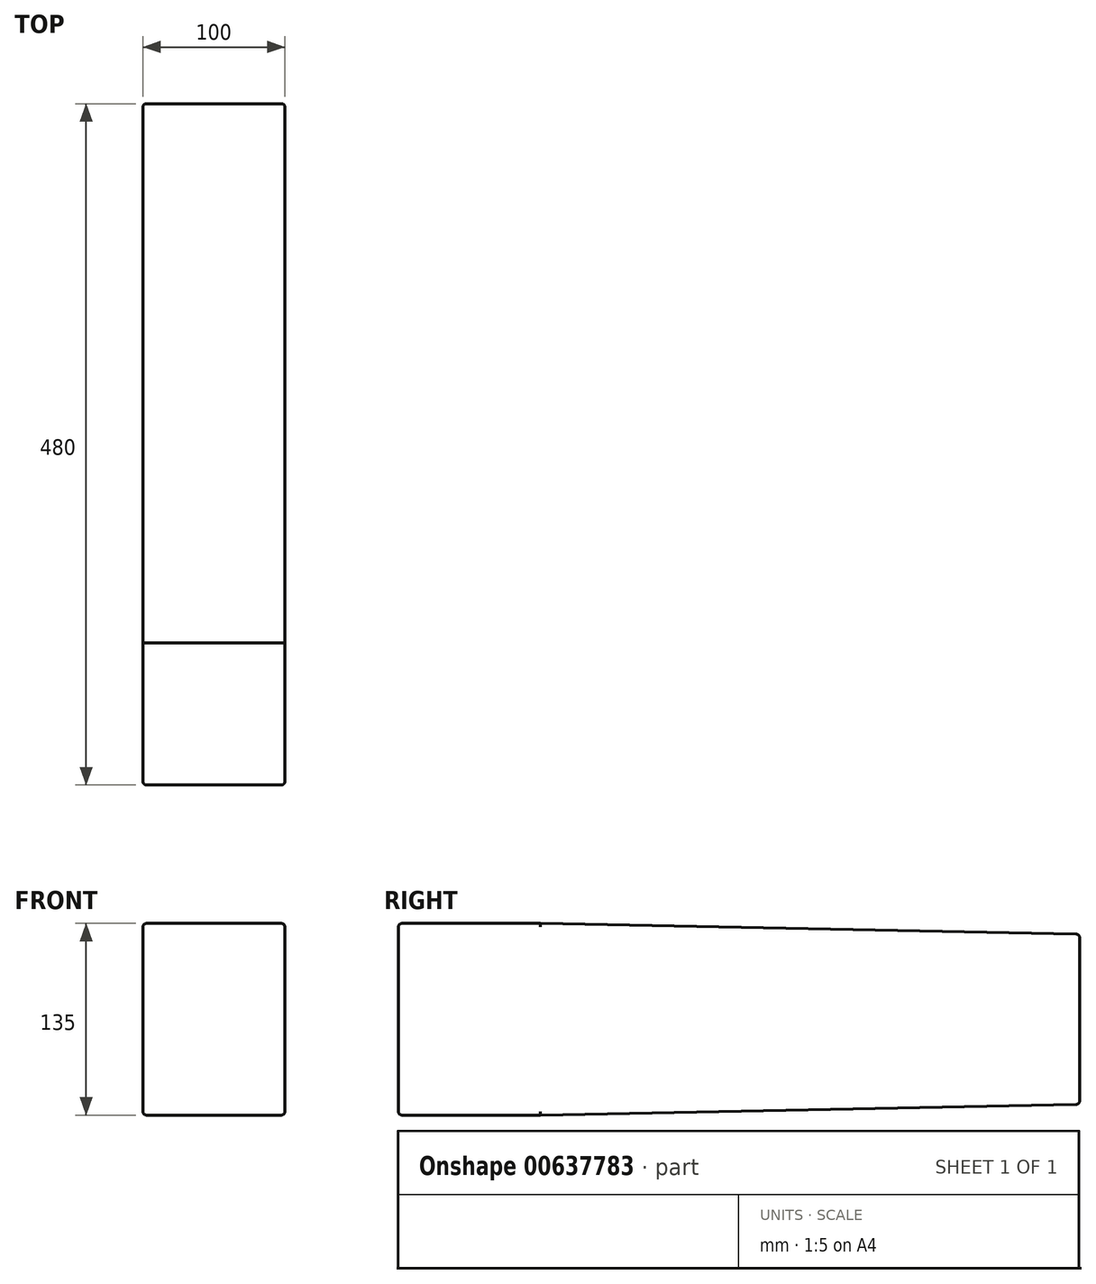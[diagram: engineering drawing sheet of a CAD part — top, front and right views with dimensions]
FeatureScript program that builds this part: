
annotation { "Feature Type Name" : "Feature", "Feature Type Description" : "" }
export const myFeature = defineFeature(function(context is Context, id is Id, definition is map)
    precondition{}
    {
        {
            var Q0;
            Q0=qCreatedBy(makeId("Right.planeOp"),FACE);
            var sketch = newSketch(context, id + "F0", { "sketchPlane" : qUnion([Q0])});
            skLineSegment(sketch, "E0.bottom", {"start": v(50, 67.5) * mm, "end": v(-50, 67.5) * mm});
            skLineSegment(sketch, "E0.top", {"start": v(50, -67.5) * mm, "end": v(-50, -67.5) * mm});
            skLineSegment(sketch, "E0.left", {"start": v(50, 67.5) * mm, "end": v(50, -67.5) * mm});
            skLineSegment(sketch, "E0.right", {"start": v(-50, 67.5) * mm, "end": v(-50, -67.5) * mm});
            skPoint(sketch, "E0.middle", {"position": v(0, 0) * mm});
            skLineSegment(sketch, "E1.bottom", {"start": v(370, -60) * mm, "end": v(430, -60) * mm});
            skLineSegment(sketch, "E1.top", {"start": v(370, 60) * mm, "end": v(430, 60) * mm});
            skLineSegment(sketch, "E1.left", {"start": v(370, -60) * mm, "end": v(370, 60) * mm});
            skLineSegment(sketch, "E1.right", {"start": v(430, -60) * mm, "end": v(430, 60) * mm});
            skPoint(sketch, "E1.middle", {"position": v(400, 0) * mm});
            skLineSegment(sketch, "E2", {"start": v(50, 67.5) * mm, "end": v(430, 60) * mm});
            skLineSegment(sketch, "E3", {"start": v(50, -67.5) * mm, "end": v(430, -60) * mm});
            skSolve(sketch);
        }
        {
            var Q0;
            Q0 = qSketchRegion(id + "F0", true);
            extrude(context, id + "F1", {"entities" : qUnion([Q0]), "depth" : 100 * mm, "offsetDistance" : 25 * mm});
        }
        {
            var Q0;
            Q0=makeQuery(id+"F1.opExtrude","CAP_EDGE",EDGE,{"disambiguationData":[OSD([sQuery(id+"F0.wireOp",EDGE,"E2")])],"isStart":false});
            var Q1;
            Q1=makeQuery(id+"F1.opExtrude","CAP_EDGE",EDGE,{"disambiguationData":[OSD([sQuery(id+"F0.wireOp",EDGE,"E1.right")])],"isStart":false});
            var Q2;
            Q2=makeQuery(id+"F1.opExtrude","CAP_EDGE",EDGE,{"disambiguationData":[OSD([sQuery(id+"F0.wireOp",EDGE,"E3")])],"isStart":false});
            var Q3;
            Q3=makeQuery(id+"F1.opExtrude","CAP_EDGE",EDGE,{"disambiguationData":[OSD([sQuery(id+"F0.wireOp",EDGE,"E0.bottom")])],"isStart":false});
            var Q4;
            Q4=makeQuery(id+"F1.opExtrude","CAP_EDGE",EDGE,{"disambiguationData":[OSD([sQuery(id+"F0.wireOp",EDGE,"E0.right")])],"isStart":false});
            var Q5;
            Q5=makeQuery(id+"F1.opExtrude","CAP_EDGE",EDGE,{"disambiguationData":[OSD([sQuery(id+"F0.wireOp",EDGE,"E0.top")])],"isStart":false});
            var Q6;
            Q6=makeQuery(id+"F1.opExtrude","SWEPT_EDGE",EDGE,{"disambiguationData":[OSD([sQuery(id+"F0.wireOp",EDGE,"E0.top"),sQuery(id+"F0.wireOp",EDGE,"E0.right")])]});
            var Q7;
            Q7=makeQuery(id+"F1.opExtrude","CAP_EDGE",EDGE,{"disambiguationData":[OSD([sQuery(id+"F0.wireOp",EDGE,"E0.right")])],"isStart":true});
            var Q8;
            Q8=makeQuery(id+"F1.opExtrude","CAP_EDGE",EDGE,{"disambiguationData":[OSD([sQuery(id+"F0.wireOp",EDGE,"E0.bottom")])],"isStart":true});
            var Q9;
            Q9=makeQuery(id+"F1.opExtrude","CAP_EDGE",EDGE,{"disambiguationData":[OSD([sQuery(id+"F0.wireOp",EDGE,"E3")])],"isStart":true});
            var Q10;
            Q10=makeQuery(id+"F1.opExtrude","CAP_EDGE",EDGE,{"disambiguationData":[OSD([sQuery(id+"F0.wireOp",EDGE,"E0.top")])],"isStart":true});
            var Q11;
            Q11=makeQuery(id+"F1.opExtrude","SWEPT_EDGE",EDGE,{"disambiguationData":[OSD([sQuery(id+"F0.wireOp",EDGE,"E1.bottom"),sQuery(id+"F0.wireOp",EDGE,"E1.right"),sQuery(id+"F0.wireOp",EDGE,"E3")])]});
            var Q12;
            Q12=makeQuery(id+"F1.opExtrude","CAP_EDGE",EDGE,{"disambiguationData":[OSD([sQuery(id+"F0.wireOp",EDGE,"E1.right")])],"isStart":true});
            var Q13;
            Q13=makeQuery(id+"F1.opExtrude","SWEPT_EDGE",EDGE,{"disambiguationData":[OSD([sQuery(id+"F0.wireOp",EDGE,"E1.top"),sQuery(id+"F0.wireOp",EDGE,"E1.right"),sQuery(id+"F0.wireOp",EDGE,"E2")])]});
            var Q14;
            Q14=makeQuery(id+"F1.opExtrude","CAP_EDGE",EDGE,{"disambiguationData":[OSD([sQuery(id+"F0.wireOp",EDGE,"E2")])],"isStart":true});
            var Q15;
            Q15=makeQuery(id+"F1.opExtrude","SWEPT_EDGE",EDGE,{"disambiguationData":[OSD([sQuery(id+"F0.wireOp",EDGE,"E0.bottom"),sQuery(id+"F0.wireOp",EDGE,"E0.right")])]});
            fillet(context, id + "F2", {"entities" : qUnion([Q0, Q1, Q2, Q3, Q4, Q5, Q6, Q7, Q8, Q9, Q10, Q11, Q12, Q13, Q14, Q15]), "radius" : 2.5 * mm, "tangentPropagation" : true, "allowEdgeOverflow" : false});
        }
    });
